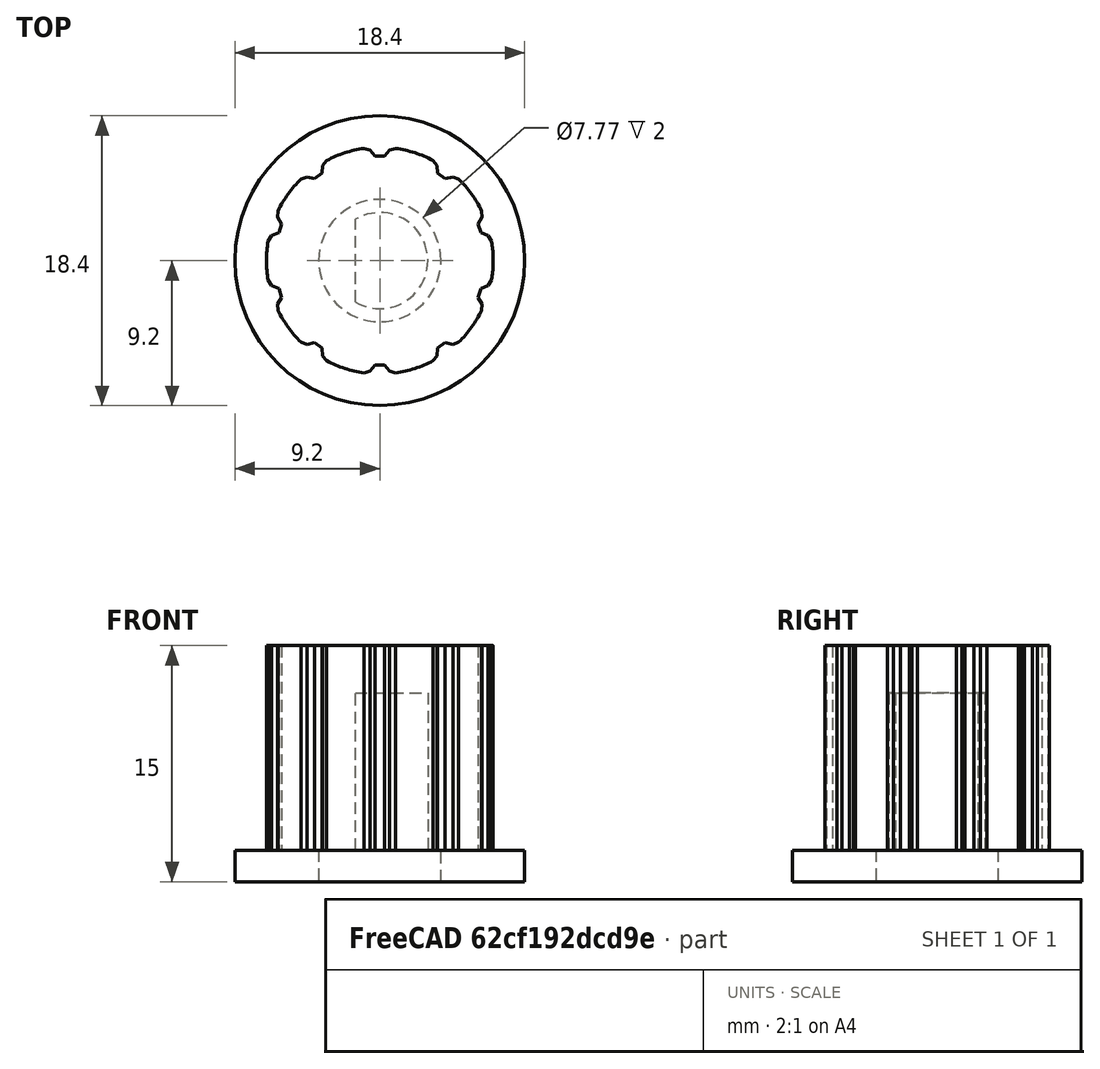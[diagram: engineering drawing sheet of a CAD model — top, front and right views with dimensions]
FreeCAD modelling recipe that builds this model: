
FCSTD DOCUMENT  (FreeCAD 1.1R43087 (Git))
Label: knob_rotary
License: All rights reserved
LicenseURL: https://en.wikipedia.org/wiki/All_rights_reserved
objects: Sketcher::SketchObject×4, PartDesign::Pocket×3, Measure::MeasureDistanceDetached×2, Mesh::Feature×1, PartDesign::Revolution×1, PartDesign::PolarPattern×1, PartDesign::Body×1, App::Point×1
note: 23 computed .brp shape members not serialized (recipe doc carries the construction recipe); baked Part::Feature solids carry a one-line shape summary decoded from their .brp

FEATURE [Mesh::Feature] knob_Dshaft_15mmx6mmv1_3  label="knob_Dshaft_15mmx6mmv1.3"
FEATURE [Measure::MeasureDistanceDetached] Distance  label="Distance: ١٩٫٥٥ mm"
  Distance = 19.5494
  DistanceX = 19.5198
  DistanceY = 1.06998
  DistanceZ = 0.118168
  Position1 = (9.82352,0.900112,1.88183)
  Position2 = (-9.69625,-0.169865,2)
FEATURE [Measure::MeasureDistanceDetached] Distance001  label="Distance: ٢٫١١ mm"
  Distance = 2.11206
  DistanceX = 2.03227
  DistanceY = 0.575023
  DistanceZ = 0
  Position1 = (-2.86569,6.56659,15)
  Position2 = (-0.833419,7.14161,15)
FEATURE [Sketcher::SketchObject] Sketch
  ArcFitTolerance = 0
  AttachmentSupport = -> [XZ_Plane]
  ExternalTypes = [0]
  FullyConstrained = true
  MakeInternals = false
  MapMode = 5
  Placement = pos=(0,0,0) rot=(1,0,0;1.5708rad)
  sketch-geometry (6):
    g0: LineSegment StartX=0 StartY=0 StartZ=0 EndX=9.2 EndY=0 EndZ=0
    g1: LineSegment StartX=9.2 StartY=0 StartZ=0 EndX=9.2 EndY=2 EndZ=0
    g2: LineSegment StartX=9.2 StartY=2 StartZ=0 EndX=7.2 EndY=2 EndZ=0
    g3: LineSegment StartX=7.2 StartY=2 StartZ=0 EndX=7.2 EndY=15 EndZ=0
    g4: LineSegment StartX=7.2 StartY=15 StartZ=0 EndX=0 EndY=15 EndZ=0
    g5: LineSegment StartX=0 StartY=15 StartZ=0 EndX=0 EndY=0 EndZ=0
  constraints (18):
    c: PointOnObject(g0,g-1)
    c: Horizontal(g2)
    c: Horizontal(g4)
    c: Coincident(g5,g4)
    c: Coincident(g5,g0)
    c: Distance(g1) = 2
    c: Vertical(g1)
    c: Vertical(g3)
    c: Vertical(g5)
    c: Distance(g5) = 15
    c: Distance(g4) = 7.2
    c: Coincident(g0,g-1)
    c: Coincident(g1,g2)
    c: Coincident(g1,g0)
    c: Coincident(g3,g4)
    c: Coincident(g2,g3)
    c: Distance(g2) = 2
    c: Distance(g0,g0) = 9.2
FEATURE [PartDesign::Revolution] Revolution
  Angle = 360
  Angle2 = 60
  Axis = (0,2e-16,1)
  Base = (0,0,0)
  Placement = pos=(0,0,0) rot=(1,0,0;1.5708rad)
  Profile = -> Sketch
  ReferenceAxis = -> Sketch [V_Axis]
  Reversed = true
  Suppressed = false
  Type = 0
FEATURE [Sketcher::SketchObject] Sketch001
  ArcFitTolerance = 0
  AttachmentSupport = -> [Revolution]
  ExternalGeometry = -> [Revolution]
  ExternalTypes = [0]
  FullyConstrained = false
  MakeInternals = false
  MapMode = 5
  Placement = pos=(0,6.6e-15,15) rot=(0,0,1;3.14159rad)
  sketch-geometry (10):
    g0: Circle [constr] CenterX=0 CenterY=0 CenterZ=0 NormalX=0 NormalY=0 NormalZ=1 AngleXU=0 Radius=6.65
    g1: LineSegment StartX=0.3 StartY=6.64323 StartZ=0 EndX=-0.3 EndY=6.64323 EndZ=0
    g2: LineSegment StartX=0.3 StartY=6.64323 StartZ=0 EndX=0.620902 EndY=7.02567 EndZ=0
    g3: LineSegment StartX=0.620902 StartY=7.02567 StartZ=0 EndX=1.00727 EndY=7.12919 EndZ=0
    g4: LineSegment StartX=-0.3 StartY=6.64323 StartZ=0 EndX=-0.620902 EndY=7.02567 EndZ=0
    g5: LineSegment StartX=-0.620902 StartY=7.02567 StartZ=0 EndX=-1.00727 EndY=7.12919 EndZ=0
    g6: ArcOfCircle CenterX=0 CenterY=0 CenterZ=0 NormalX=0 NormalY=0 NormalZ=1 AngleXU=0 Radius=7.2 StartAngle=1.43044 EndAngle=1.71116
    g7: LineSegment [constr] StartX=0 StartY=0 StartZ=0 EndX=11.2212 EndY=0 EndZ=0
    g8: GeomPoint [constr] X=6.65 Y=0 Z=0
    g9: GeomPoint [constr] X=7.2 Y=0 Z=0
  constraints (26):
    c: Coincident(g0,g-1)
    c: PointOnObject(g1,g0)
    c: PointOnObject(g1,g0)
    c: Horizontal(g1)
    c: Coincident(g2,g1)
    c: Coincident(g3,g2)
    c: PointOnObject(g3,g-3)
    c: Coincident(g4,g1)
    c: Coincident(g5,g4)
    c: Coincident(g6,g0)
    c: Coincident(g6,g5)
    c: Coincident(g6,g3)
    c: Angle(g2,g3) = 2.53073
    c: Angle(g5,g4) = 2.53073
    c: Angle(g2,g1) = 2.26893
    c: Distance(g1) = 0.6
    c: Distance(g5) = 0.4
    c: Equal(g2,g4)
    c: Equal(g3,g5)
    c: Coincident(g7,g6)
    c: Horizontal(g7)
    c: PointOnObject(g8,g7)
    c: PointOnObject(g8,g0)
    c: PointOnObject(g9,g7)
    c: PointOnObject(g9,g-3)
    c: Distance(g9,g8) = 0.55
FEATURE [PartDesign::Pocket] Pocket
  BaseFeature = -> Revolution
  Direction = (0,0,-1)
  Length = 0
  Length2 = 5
  Placement = pos=(0,0,0) rot=(1,0,0;1.5708rad)
  Profile = -> Sketch001
  ReferenceAxis = -> Sketch001 [N_Axis]
  SideType = 0
  Suppressed = false
  Type = 3
  Type2 = 0
  UpToFace = -> Revolution [Face3]
FEATURE [PartDesign::PolarPattern] PolarPattern
  Angle = 360
  Axis = -> Sketch [V_Axis]
  BaseFeature = -> Pocket
  Mode = 0
  Occurrences = 10
  Offset = 120
  Originals = -> [Pocket]
  Placement = pos=(0,0,0) rot=(1,0,0;1.5708rad)
  Suppressed = false
  TransformMode = 0
FEATURE [Sketcher::SketchObject] Sketch002
  ArcFitTolerance = 0
  AttachmentSupport = -> [PolarPattern]
  ExternalTypes = [0]
  FullyConstrained = true
  MakeInternals = false
  MapMode = 5
  Placement = pos=(0,0,0) rot=(1,0,0;3.14159rad)
  sketch-geometry (1):
    g0: Circle CenterX=0 CenterY=0 CenterZ=0 NormalX=0 NormalY=0 NormalZ=1 AngleXU=0 Radius=3.88254
  constraints (2):
    c: Coincident(g0,g-1)
    c: Diameter(g0) = 7.76508
FEATURE [PartDesign::Pocket] Pocket001
  BaseFeature = -> PolarPattern
  Direction = (0,0,1)
  Length = 2
  Length2 = 5
  Placement = pos=(0,0,0) rot=(1,0,0;1.5708rad)
  Profile = -> Sketch002
  ReferenceAxis = -> Sketch002 [N_Axis]
  SideType = 0
  Suppressed = false
  Type = 0
  Type2 = 0
FEATURE [Sketcher::SketchObject] Sketch003
  ArcFitTolerance = 0
  AttachmentSupport = -> [Pocket001]
  ExternalTypes = [0]
  FullyConstrained = true
  MakeInternals = false
  MapMode = 5
  Placement = pos=(0,0,2) rot=(1,0,0;3.14159rad)
  sketch-geometry (3):
    g0: ArcOfCircle CenterX=0 CenterY=0 CenterZ=0 NormalX=0 NormalY=0 NormalZ=1 AngleXU=0 Radius=3.05 StartAngle=4.1793 EndAngle=8.38707
    g1: LineSegment StartX=-1.55 StartY=2.62679 StartZ=0 EndX=-1.55 EndY=-2.62679 EndZ=0
    g2: GeomPoint X=3.05 Y=0 Z=0
  constraints (8):
    c: Coincident(g0,g-1)
    c: Vertical(g1)
    c: Diameter(g0) = 6.1
    c: Coincident(g0,g1)
    c: Coincident(g0,g1)
    c: PointOnObject(g2,g0)
    c: PointOnObject(g2,g-1)
    c: Distance(g2,g1) = 4.6
FEATURE [PartDesign::Pocket] Pocket002
  BaseFeature = -> Pocket001
  Direction = (0,0,1)
  Length = 10
  Length2 = 5
  Placement = pos=(0,0,0) rot=(1,0,0;1.5708rad)
  Profile = -> Sketch003
  ReferenceAxis = -> Sketch003 [N_Axis]
  SideType = 0
  Suppressed = false
  Type = 0
  Type2 = 0
FEATURE [PartDesign::Body] Body
  AllowCompound = false
  Group = -> [Sketch,Revolution,Sketch001,Pocket,PolarPattern,Sketch002,Sketch003,Pocket001,Pocket002]
  Origin = -> Origin
  Tip = -> Pocket002
FEATURE [App::Point] Origin001  label="Origin"
  Role = Origin
